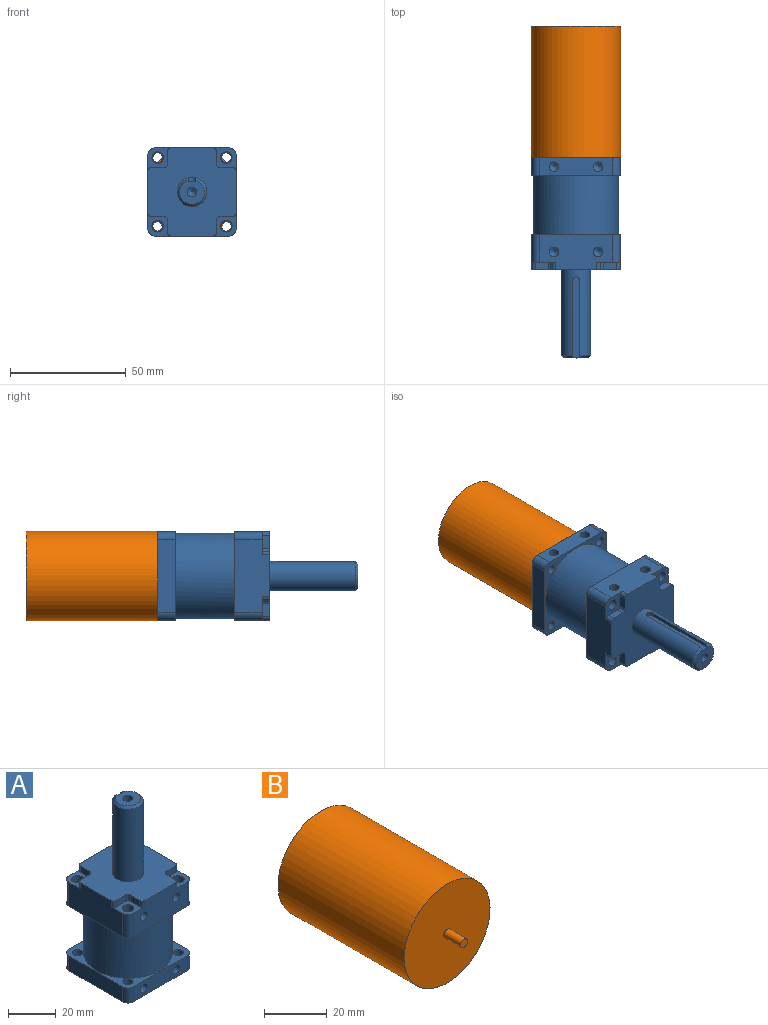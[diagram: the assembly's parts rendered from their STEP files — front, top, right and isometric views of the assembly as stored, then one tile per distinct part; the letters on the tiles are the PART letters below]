
ASSEMBLY  parts=2 mates=1
PART A: 82 faces, bbox 38.1x38.1x86.4 mm
  f0: plane 38.1x38.1mm, normal (0,0,1), area 312.3mm2, adj f21,f22,f23,f24,f25,f26,f27,f28
  f1: plane 38.1x38.1mm, normal (0,0,-1), area 1387.5mm2, adj f22,f23,f24,f25,f26,f27,f28,f29
  f2: cylinder r=3.17mm len=12.07mm, axis (0,0,-1), area 60.2mm2, adj f6,f11,f12,f41
  f3: cylinder r=3.17mm len=12.07mm, axis (0,0,-1), area 60.2mm2, adj f6,f9,f12,f38
  f4: cylinder r=3.17mm len=12.07mm, axis (0,0,-1), area 60.2mm2, adj f6,f9,f10,f35
  f5: cylinder r=3.17mm len=12.07mm, axis (0,0,-1), area 60.2mm2, adj f6,f10,f11,f32
  f6: plane 38.1x38.1mm, normal (0,0,-1), area 289.4mm2, adj f2,f3,f4,f5,f9,f10,f11,f12
  f7: cylinder r=1.59mm len=3.18mm, axis (0,-1,0), area 7.9mm2, adj f13,f16,f17,f18
  f8: plane 38.1x38.1mm, normal (0,0,1), area 1034mm2, adj f9,f10,f11,f12,f13,f30,f31,f33
  f9: plane 31.75x15.24mm, normal (1,0,0), area 440.5mm2, adj f3,f4,f6,f8,f35,f38,f44,f45
  f10: plane 31.75x15.24mm, normal (0,1,0), area 412.8mm2, adj f4,f5,f6,f8,f32,f35,f47,f51
  f11: plane 31.75x15.24mm, normal (-1,0,0), area 440.5mm2, adj f2,f5,f6,f8,f32,f41,f50,f52
  f12: plane 31.75x15.24mm, normal (0,-1,0), area 412.8mm2, adj f2,f3,f6,f8,f38,f41,f42,f48
  f13: cylinder r=6.35mm len=37.1mm, axis (0,0,-1), area 1372.2mm2, adj f7,f8,f15,f16,f17
  f14: plane 10.7x10.46mm, normal (0,0,1), area 73.8mm2, adj f15,f16,f17,f18,f20
  f15: cone r=5.35mm half-angle=45deg, axis (0,0,-1), area 47.4mm2, adj f13,f14,f16,f17
  f16: plane 33.44x1.61mm, normal (-1,0,0), area 52.5mm2, adj f7,f13,f14,f15,f18
  f17: plane 33.44x1.61mm, normal (1,0,0), area 52.5mm2, adj f7,f13,f14,f15,f18
  f18: plane 35x3.18mm, normal (0,1,0), area 110mm2, adj f7,f14,f16,f17
  f19: cone r=2.1mm half-angle=59deg, axis (0,0,1), area 16.2mm2, adj f20
  f20: cylinder r=2.1mm len=14mm, axis (0,0,1), area 184.7mm2, adj f14,f19
  f21: cylinder r=18.5mm len=37mm, axis (0,0,1), area 2952.5mm2, adj f0,f6,f54,f56,f58,f60
  f22: cylinder r=3.17mm len=7.62mm, axis (0,0,1), area 38mm2, adj f0,f1,f23,f29
  f23: plane 31.75x7.62mm, normal (0,-1,0), area 214.2mm2, adj f0,f1,f22,f24,f79,f81
  f24: cylinder r=3.17mm len=7.62mm, axis (0,0,1), area 38mm2, adj f0,f1,f23,f25
  f25: plane 31.75x7.62mm, normal (-1,0,0), area 241.9mm2, adj f0,f1,f24,f26
  f26: cylinder r=3.17mm len=7.62mm, axis (0,0,1), area 38mm2, adj f0,f1,f25,f27
  f27: plane 31.75x7.62mm, normal (0,1,0), area 214.2mm2, adj f0,f1,f26,f28,f71,f73
  f28: cylinder r=3.17mm len=7.62mm, axis (0,0,1), area 38mm2, adj f0,f1,f27,f29
  f29: plane 31.75x7.62mm, normal (1,0,0), area 241.9mm2, adj f0,f1,f22,f28
  f30: plane 5.5x3.18mm, normal (-1,0,0), area 17.5mm2, adj f8,f32,f51,f53
  f31: plane 5.5x3.18mm, normal (0,1,0), area 17.5mm2, adj f8,f32,f52,f53
  f32: plane 10x10mm, normal (0,0,1), area 50.9mm2, adj f5,f10,f11,f30,f31,f51,f52,f53
  f33: plane 5.5x3.18mm, normal (0,1,0), area 17.5mm2, adj f8,f35,f45,f46
  f34: plane 5.5x3.18mm, normal (1,0,0), area 17.5mm2, adj f8,f35,f46,f47
  f35: plane 10x10mm, normal (0,0,1), area 50.9mm2, adj f4,f9,f10,f33,f34,f45,f46,f47
  f36: plane 5.5x3.18mm, normal (1,0,0), area 17.5mm2, adj f8,f38,f42,f43
  f37: plane 5.5x3.18mm, normal (0,-1,0), area 17.5mm2, adj f8,f38,f43,f44
  f38: plane 10x10mm, normal (0,0,1), area 50.9mm2, adj f3,f9,f12,f36,f37,f42,f43,f44
  f39: plane 5.5x3.18mm, normal (0,-1,0), area 17.5mm2, adj f8,f41,f49,f50
  f40: plane 5.5x3.18mm, normal (-1,0,0), area 17.5mm2, adj f8,f41,f48,f49
  f41: plane 10x10mm, normal (0,0,1), area 50.9mm2, adj f2,f11,f12,f39,f40,f48,f49,f50
  f42: cylinder r=1.5mm len=3.18mm, axis (0,0,1), area 7.5mm2, adj f8,f12,f36,f38
  f43: cylinder r=1.5mm len=3.18mm, axis (0,0,-1), area 7.5mm2, adj f8,f36,f37,f38
  f44: cylinder r=1.5mm len=3.18mm, axis (0,0,1), area 7.5mm2, adj f8,f9,f37,f38
  f45: cylinder r=1.5mm len=3.18mm, axis (0,0,1), area 7.5mm2, adj f8,f9,f33,f35
  f46: cylinder r=1.5mm len=3.18mm, axis (0,0,-1), area 7.5mm2, adj f8,f33,f34,f35
  f47: cylinder r=1.5mm len=3.18mm, axis (0,0,1), area 7.5mm2, adj f8,f10,f34,f35
  f48: cylinder r=1.5mm len=3.18mm, axis (0,0,1), area 7.5mm2, adj f8,f12,f40,f41
  f49: cylinder r=1.5mm len=3.18mm, axis (0,0,-1), area 7.5mm2, adj f8,f39,f40,f41
  f50: cylinder r=1.5mm len=3.18mm, axis (0,0,1), area 7.5mm2, adj f8,f11,f39,f41
  f51: cylinder r=1.5mm len=3.18mm, axis (0,0,1), area 7.5mm2, adj f8,f10,f30,f32
  f52: cylinder r=1.5mm len=3.18mm, axis (0,0,1), area 7.5mm2, adj f8,f11,f31,f32
  f53: cylinder r=1.5mm len=3.18mm, axis (0,0,-1), area 7.5mm2, adj f8,f30,f31,f32
  f54: plane 0.78x0.78mm, normal (0,0,1), area 0.1mm2, adj f21,f55
  f55: cylinder r=2.5mm len=12.07mm, axis (0,0,1), area 189.5mm2, adj f6,f32,f54
  f56: plane 0.78x0.78mm, normal (0,0,1), area 0.1mm2, adj f21,f57
  f57: cylinder r=2.5mm len=12.07mm, axis (0,0,1), area 189.5mm2, adj f6,f41,f56
  f58: plane 0.78x0.78mm, normal (0,0,1), area 0.1mm2, adj f21,f59
  f59: cylinder r=2.5mm len=12.07mm, axis (0,0,1), area 189.5mm2, adj f6,f38,f58
  f60: plane 0.78x0.78mm, normal (0,0,1), area 0.1mm2, adj f21,f61
  f61: cylinder r=2.5mm len=12.07mm, axis (0,0,1), area 189.5mm2, adj f6,f35,f60
  f62: cylinder r=2.1mm len=7.62mm, axis (0,0,1), area 100.5mm2, adj f0,f1
  f63: cylinder r=2.1mm len=7.62mm, axis (0,0,1), area 100.5mm2, adj f0,f1
  f64: cylinder r=2.1mm len=7.62mm, axis (0,0,1), area 100.5mm2, adj f0,f1
  f65: cylinder r=2.1mm len=7.62mm, axis (0,0,1), area 100.5mm2, adj f0,f1
  f66: cone r=2.1mm half-angle=59deg, axis (0,1,0), area 16.2mm2, adj f67
  f67: cylinder r=2.1mm len=7.62mm, axis (0,1,0), area 100.5mm2, adj f10,f66
  f68: cone r=2.1mm half-angle=59deg, axis (0,1,0), area 16.2mm2, adj f69
  f69: cylinder r=2.1mm len=7.62mm, axis (0,1,0), area 100.5mm2, adj f10,f68
  f70: cone r=2.1mm half-angle=59deg, axis (0,1,0), area 16.2mm2, adj f71
  f71: cylinder r=2.1mm len=7.62mm, axis (0,1,0), area 100.5mm2, adj f27,f70
  f72: cone r=2.1mm half-angle=59deg, axis (0,1,0), area 16.2mm2, adj f73
  f73: cylinder r=2.1mm len=7.62mm, axis (0,1,0), area 100.5mm2, adj f27,f72
  f74: cone r=2.1mm half-angle=59deg, axis (0,-1,0), area 16.2mm2, adj f75
  f75: cylinder r=2.1mm len=7.62mm, axis (0,-1,0), area 100.5mm2, adj f12,f74
  f76: cone r=2.1mm half-angle=59deg, axis (0,-1,0), area 16.2mm2, adj f77
  f77: cylinder r=2.1mm len=7.62mm, axis (0,-1,0), area 100.5mm2, adj f12,f76
  f78: cone r=2.1mm half-angle=59deg, axis (0,-1,0), area 16.2mm2, adj f79
  f79: cylinder r=2.1mm len=7.62mm, axis (0,-1,0), area 100.5mm2, adj f23,f78
  f80: cone r=2.1mm half-angle=59deg, axis (0,-1,0), area 16.2mm2, adj f81
  f81: cylinder r=2.1mm len=7.62mm, axis (0,-1,0), area 100.5mm2, adj f23,f80
PART B: 5 faces, bbox 38.6x64.5x38.6 mm
  f0: cylinder r=19.3mm len=56.9mm, axis (0,1,0), area 6901mm2, adj f1,f2
  f1: plane 38.61x38.61mm, normal (0,-1,0), area 1162.8mm2, adj f0,f3
  f2: plane 38.61x38.61mm, normal (0,1,0), area 1170.7mm2, adj f0
  f3: cylinder r=1.59mm len=7.62mm, axis (0,1,0), area 76mm2, adj f1,f4
  f4: plane 3.18x3.18mm, normal (0,-1,0), area 7.9mm2, adj f3
PLACE A rot(axis=(1,0,0),90deg) t=(55.96,-37.77,17.1)mm
PLACE B t=(55.96,52.14,17.1)mm
MATE fastened A.f13 <-> B.f0  axis (0,1,0) through (55.96,-4.75,17.1)mm
